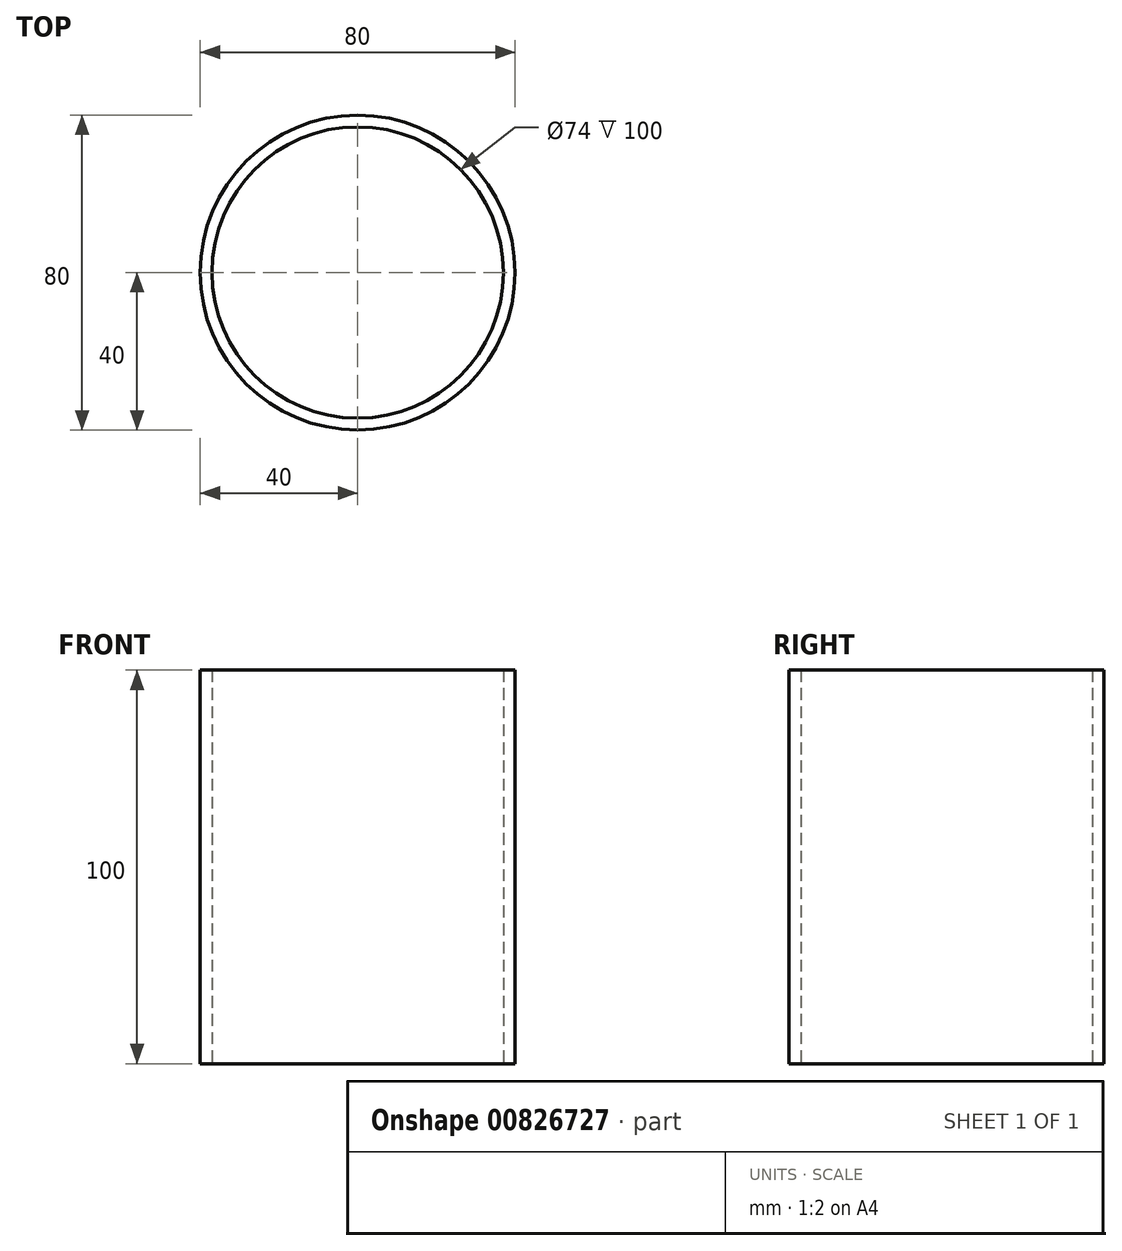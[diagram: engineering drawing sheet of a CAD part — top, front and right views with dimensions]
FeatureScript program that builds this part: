
annotation { "Feature Type Name" : "Feature", "Feature Type Description" : "" }
export const myFeature = defineFeature(function(context is Context, id is Id, definition is map)
    precondition{}
    {
        {
            var Q0;
            Q0=qCreatedBy(makeId("Top.planeOp"),FACE);
            var sketch = newSketch(context, id + "F0", { "sketchPlane" : qUnion([Q0])});
            skCircle(sketch, "E0", {"center": v(0, 0) * mm, "radius": 40 * mm});
            skCircle(sketch, "E1", {"center": v(0, 0) * mm, "radius": 37 * mm});
            skSolve(sketch);
        }
        {
            var Q0;
            Q0=makeQuery(id+"F0.imprint","IMPRINT",FACE,{"disambiguationData":[TD([[makeQuery(id+"F0.imprint","IMPRINT",EDGE,{"derivedFrom":sQuery(id+"F0.wireOp",EDGE,"E0")}),1.0]])]});
            extrude(context, id + "F1", {"entities" : qUnion([Q0]), "depth" : 100 * mm, "offsetDistance" : 25 * mm});
        }
    });
